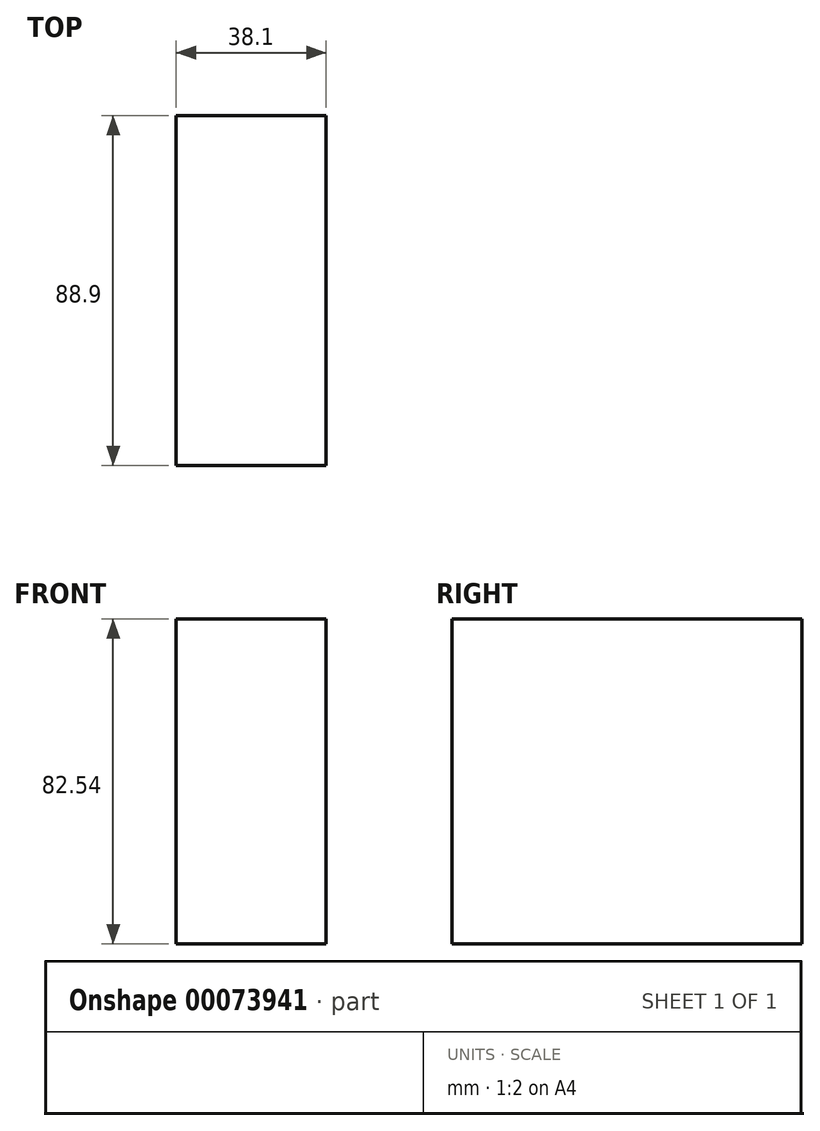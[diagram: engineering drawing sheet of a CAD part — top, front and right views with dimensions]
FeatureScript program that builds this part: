
annotation { "Feature Type Name" : "Feature", "Feature Type Description" : "" }
export const myFeature = defineFeature(function(context is Context, id is Id, definition is map)
    precondition{}
    {
        {
            var Q0;
            Q0=qCreatedBy(makeId("Top.planeOp"),FACE);
            var sketch = newSketch(context, id + "F0", { "sketchPlane" : qUnion([Q0])});
            skLineSegment(sketch, "E0.rect.bottom", {"start": v(44.45, 19.05) * mm, "end": v(-44.45, 19.05) * mm});
            skLineSegment(sketch, "E0.rect.top", {"start": v(44.45, -19.05) * mm, "end": v(-44.45, -19.05) * mm});
            skLineSegment(sketch, "E0.rect.left", {"start": v(44.45, 19.05) * mm, "end": v(44.45, -19.05) * mm});
            skLineSegment(sketch, "E0.rect.right", {"start": v(-44.45, 19.05) * mm, "end": v(-44.45, -19.05) * mm});
            skPoint(sketch, "E0.rect.middle", {"position": v(0, 0) * mm});
            skSolve(sketch);
        }
        {
            var Q0;
            Q0=makeQuery(id+"F0.imprint","IMPRINT",FACE,{"disambiguationData":[TD([[makeQuery(id+"F0.imprint","IMPRINT",EDGE,{"derivedFrom":sQuery(id+"F0.wireOp",EDGE,"E0.rect.bottom")}),1.0]])]});
            extrude(context, id + "F1", {"entities" : qUnion([Q0]), "depth" : 82.55 * mm});
        }
        {
            var Q0;
            Q0=makeQuery(id+"F1.opExtrude","SWEPT_BODY",BODY,{"disambiguationData":[OSD([sQuery(id+"F0.wireOp",EDGE,"E0.rect.bottom"),sQuery(id+"F0.wireOp",EDGE,"E0.rect.top"),sQuery(id+"F0.wireOp",EDGE,"E0.rect.left"),sQuery(id+"F0.wireOp",EDGE,"E0.rect.right")])]});
            transform(context, id + "F2", {"entities" : qUnion([Q0]), "transformType" : TransformType.TRANSLATION_3D, "dx" : 0 * mm, "dy" : 0 * mm, "dz" : 0 * mm, "makeCopy" : true});
        }
        {
            var Q0;
            Q0=makeQuery(id+"F1.opExtrude","SWEPT_BODY",BODY,{"disambiguationData":[OSD([sQuery(id+"F0.wireOp",EDGE,"E0.rect.bottom"),sQuery(id+"F0.wireOp",EDGE,"E0.rect.top"),sQuery(id+"F0.wireOp",EDGE,"E0.rect.left"),sQuery(id+"F0.wireOp",EDGE,"E0.rect.right")])]});
            deleteBodies(context, id + "F3", {"entities" : qUnion([Q0])});
        }
        {
            var Q0;
            Q0=makeQuery(id+"F2.opPattern","COPY",BODY,{"derivedFrom":makeQuery(id+"F1.opExtrude","SWEPT_BODY",BODY,{"disambiguationData":[OSD([sQuery(id+"F0.wireOp",EDGE,"E0.rect.bottom"),sQuery(id+"F0.wireOp",EDGE,"E0.rect.top"),sQuery(id+"F0.wireOp",EDGE,"E0.rect.left"),sQuery(id+"F0.wireOp",EDGE,"E0.rect.right")])]}),"instanceName":"1"});
            deleteBodies(context, id + "F4", {"entities" : qUnion([Q0])});
        }
        {
            var Q0;
            Q0=qCreatedBy(makeId("Right.planeOp"),FACE);
            var sketch = newSketch(context, id + "F5", { "sketchPlane" : qUnion([Q0])});
            skLineSegment(sketch, "E1.rect.bottom", {"start": v(-44.45, 41.28) * mm, "end": v(44.45, 41.28) * mm});
            skLineSegment(sketch, "E1.rect.top", {"start": v(-44.45, -41.27) * mm, "end": v(44.45, -41.27) * mm});
            skLineSegment(sketch, "E1.rect.left", {"start": v(-44.45, 41.28) * mm, "end": v(-44.45, -41.28) * mm});
            skLineSegment(sketch, "E1.rect.right", {"start": v(44.45, 41.28) * mm, "end": v(44.45, -41.27) * mm});
            skPoint(sketch, "E1.rect.middle", {"position": v(0, 0) * mm});
            skPoint(sketch, "E2", {"position": v(0, -41.27) * mm});
            skPoint(sketch, "E3", {"position": v(0, 41.28) * mm});
            skPoint(sketch, "E4", {"position": v(-44.45, 0) * mm});
            skPoint(sketch, "E5", {"position": v(44.45, 0) * mm});
            skSolve(sketch);
        }
        {
            var Q0;
            Q0=makeQuery(id+"F5.imprint","IMPRINT",FACE,{"disambiguationData":[TD([[makeQuery(id+"F5.imprint","IMPRINT",EDGE,{"derivedFrom":sQuery(id+"F5.wireOp",EDGE,"E1.rect.bottom")}),-1.0]])]});
            extrude(context, id + "F6", {"entities" : qUnion([Q0]), "depth" : 38.1 * mm});
        }
    });
